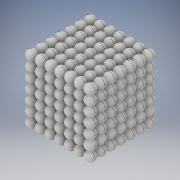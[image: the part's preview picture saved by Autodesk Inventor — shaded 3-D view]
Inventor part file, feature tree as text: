
AUTODESK INVENTOR PART (.ipt)
format: ipt  version: 2018.2 (Build 222227000, 227)  size: 22,889,984 bytes
history: native  units: in
note: dims shown in document units (in); Inventor stores cm internally (conversion verified against a paired STEP export)
features: other x76, plane x21, mirror x19, sketch x7, projected_geometry x2
ambient origin geometry x8: Origin, YZ Plane, XZ Plane, XY Plane, X Axis, Y Axis, Z Axis, Center Point
bodies: Solid8 (feature_tree), Solid9 (feature_tree), Solid10 (feature_tree), Solid11 (feature_tree), Solid12 (feature_tree), Solid13 (feature_tree), Solid14 (feature_tree), Solid24 (feature_tree), Solid23 (feature_tree), Solid22 (feature_tree), Solid45 (feature_tree), Solid46 (feature_tree), Solid47 (feature_tree), Solid48 (feature_tree), Solid49 (feature_tree), Solid50 (feature_tree), Solid51 (feature_tree), Solid52 (feature_tree), Solid53 (feature_tree), Solid59 (feature_tree), Solid58 (feature_tree), Solid57 (feature_tree), Solid56 (feature_tree), Solid55 (feature_tree), Solid54 (feature_tree), Solid60 (feature_tree), Solid68 (feature_tree), Solid66 (feature_tree), Solid64 (feature_tree), Solid70 (feature_tree), Solid71 (feature_tree), Solid77 (feature_tree), Solid72 (feature_tree), Solid78 (feature_tree), Solid76 (feature_tree), Solid75 (feature_tree), Solid74 (feature_tree), Solid73 (feature_tree), Solid69 (feature_tree), Solid67 (feature_tree), Solid65 (feature_tree), Solid91 (feature_tree), Solid88 (feature_tree), Solid87 (feature_tree), Solid86 (feature_tree), Solid83 (feature_tree), Solid84 (feature_tree), Solid85 (feature_tree), Solid81 (feature_tree), Solid82 (feature_tree), Solid80 (feature_tree), Solid79 (feature_tree), Solid89 (feature_tree), Solid90 (feature_tree), Solid92 (feature_tree), Solid93 (feature_tree), Solid94 (feature_tree), Solid95 (feature_tree), Solid96 (feature_tree), Solid97 (feature_tree), Solid98 (feature_tree), Solid99 (feature_tree), Solid100 (feature_tree), Solid101 (feature_tree), Solid102 (feature_tree), Solid103 (feature_tree), Solid104 (feature_tree), Solid1 (feature_tree), Solid2 (feature_tree), Solid3 (feature_tree), Solid4 (feature_tree), Solid5 (feature_tree), Solid6 (feature_tree), Solid7 (feature_tree), Solid15 (feature_tree), Solid16 (feature_tree), Solid17 (feature_tree), Solid18 (feature_tree), Solid19 (feature_tree), Solid20 (feature_tree), Solid21 (feature_tree), Solid25 (feature_tree), Solid26 (feature_tree), Solid27 (feature_tree), Solid28 (feature_tree), Solid29 (feature_tree), Solid30 (feature_tree), Solid31 (feature_tree), Solid32 (feature_tree), Solid39 (feature_tree), Solid40 (feature_tree), Solid41 (feature_tree), Solid42 (feature_tree), Solid43 (feature_tree), Solid44 (feature_tree), Solid61 (feature_tree), Solid62 (feature_tree), Solid63 (feature_tree)
feature tree (125):
  sketch  "Sketch1"  dims[d0=2.7559in]
  other  "Form1"
  plane  "Work Plane1"
  mirror  "Mirror1"
  plane  "Work Plane2"
  mirror  "Mirror2"
  plane  "Work Plane3"
  mirror  "Mirror3"
  plane  "Work Plane4"
  sketch  "Sketch2"  dims[d3=0.1969in]
  other  "Form2"
  plane  "Work Plane5"
  mirror  "Mirror4"
  plane  "Work Plane6"
  mirror  "Mirror5"
  plane  "Work Plane7"
  mirror  "Mirror6"
  plane  "Work Plane8"
  sketch  "Sketch4"  dims[d4=0.1969in]
  other  "Form3"
  other  "Form4"
  plane  "Work Plane9"
  sketch  "Sketch5"  dims[d5=0.3937in]
  other  "Form5"
  other  "Form7"
  plane  "Work Plane18"
  plane  "Work Plane11"
  plane  "Work Plane13"
  mirror  "Mirror8"
  plane  "Work Plane14"
  mirror  "Mirror9"
  plane  "Work Plane15"
  mirror  "Mirror10"
  plane  "Work Plane16"
  mirror  "Mirror11"
  plane  "Work Plane17"
  mirror  "Mirror12"
  mirror  "Mirror7"
  mirror  "Mirror13"
  mirror  "Mirror14"
  plane  "Work Plane20"
  plane  "Work Plane21"
  sketch  "Sketch7"  dims[d6=0.3937in]
  other  "Form8"
  sketch  "Sketch8"  dims[d7=0.3937in]
  other  "Form9"
  sketch  "Sketch9"  dims[d8=0.3937in d9=0.3937in d10=0.1969in d11=0.3937in d12=0.7874in d13=0.9843in d14=2.7559in d15=0.1969in d16=0.1969in d17=0.3937in d18=0.3937in d19=0.3937in d20=0.3937in d21=0.3937in d22=0.1969in d23=0.3937in d24=0.7874in d25=0.9843in d26=0.3937in d27=0.3937in d28=0.3937in d29=0.3937in d30=0.3937in d31=0.3937in d32=0.3937in d33=2.7559in d34=0.3937in d35=0.3937in d36=0.3937in d37=0.3937in d38=0.3937in d39=0.3937in d40=7.874in d41=-0.3937in d43=0.1969in d44=-0.3937in d45=-0.3937in d46=-0.7874in d47=0.1969in d48=0.1969in d50=-0.1969in d51=2.3622in d52=0.3937in d53=0.1969in d54=-0.3937in d70=-0.3937in]
  other  "Form10"
  plane  "Work Plane22"
  mirror  "Mirror15"
  mirror  "Mirror16"
  mirror  "Mirror17"
  plane  "Work Plane23"
  mirror  "Mirror18"
  mirror  "Mirror19"
  other  "Pattern of Solid1:1"
  other  "Pattern of Solid2:2"
  other  "Pattern of Solid3:3"
  other  "Pattern of Solid4:4"
  other  "Pattern of Solid5:5"
  other  "Pattern of Solid6:6"
  other  "Pattern of Solid7:7"
  other  "Pattern of Solid15:8"
  other  "Pattern of Solid8:9"
  other  "Pattern of Solid1:10"
  projected_geometry  "Projected Loop1"
  plane  "Work Plane10"
  other  "Pattern of Solid15:11"
  other  "Pattern of Solid24:12"
  other  "Pattern of Solid25:13"
  other  "Pattern of Solid45:14"
  other  "Pattern of Solid46:15"
  other  "Pattern of Solid47:16"
  other  "Pattern of Solid48:17"
  other  "Pattern of Solid49:18"
  other  "Pattern of Solid50:19"
  other  "Pattern of Solid7:20"
  other  "Pattern of Solid6:21"
  other  "Pattern of Solid5:22"
  other  "Pattern of Solid4:23"
  other  "Pattern of Solid3:24"
  other  "Pattern of Solid2:25"
  other  "Pattern of Solid31:26"
  projected_geometry  "Projected Loop10"
  other  "Pattern of Solid15:27"
  other  "Pattern of Solid8:28"
  other  "Pattern of Solid1:29"
  other  "Pattern of Solid23:30"
  other  "Pattern of Solid22:31"
  other  "Pattern of Solid29:32"
  other  "Pattern of Solid60:33"
  other  "Pattern of Solid31:34"
  other  "Pattern of Solid28:35"
  other  "Pattern of Solid27:36"
  other  "Pattern of Solid26:37"
  other  "Pattern of Solid25:38"
  other  "Pattern of Solid24:39"
  other  "Pattern of Solid9:40"
  other  "Pattern of Solid2:41"
  other  "Pattern of Solid47:42"
  other  "Pattern of Solid74:43"
  other  "Pattern of Solid75:44"
  other  "Pattern of Solid76:45"
  other  "Pattern of Solid77:46"
  other  "Pattern of Solid72:47"
  other  "Pattern of Solid78:48"
  other  "Pattern of Solid70:49"
  other  "Pattern of Solid71:50"
  other  "Pattern of Solid64:51"
  other  "Pattern of Solid66:52"
  other  "Pattern of Solid69:53"
  other  "Pattern of Solid45:54"
  other  "Pattern of Solid91:55"
  other  "Pattern of Solid88:56"
  other  "Pattern of Solid87:57"
  other  "Pattern of Solid86:58"
  other  "Pattern of Solid83:59"
  other  "Pattern of Solid84:60"
  other  "Pattern of Solid85:61"
  other  "Pattern of Solid81:62"
  other  "Pattern of Solid82:63"
  other  "Pattern of Solid80:64"
  other  "Pattern of Solid79:65"
  other  "Pattern of Solid90:66"
  other  "Pattern of Solid46:67"
